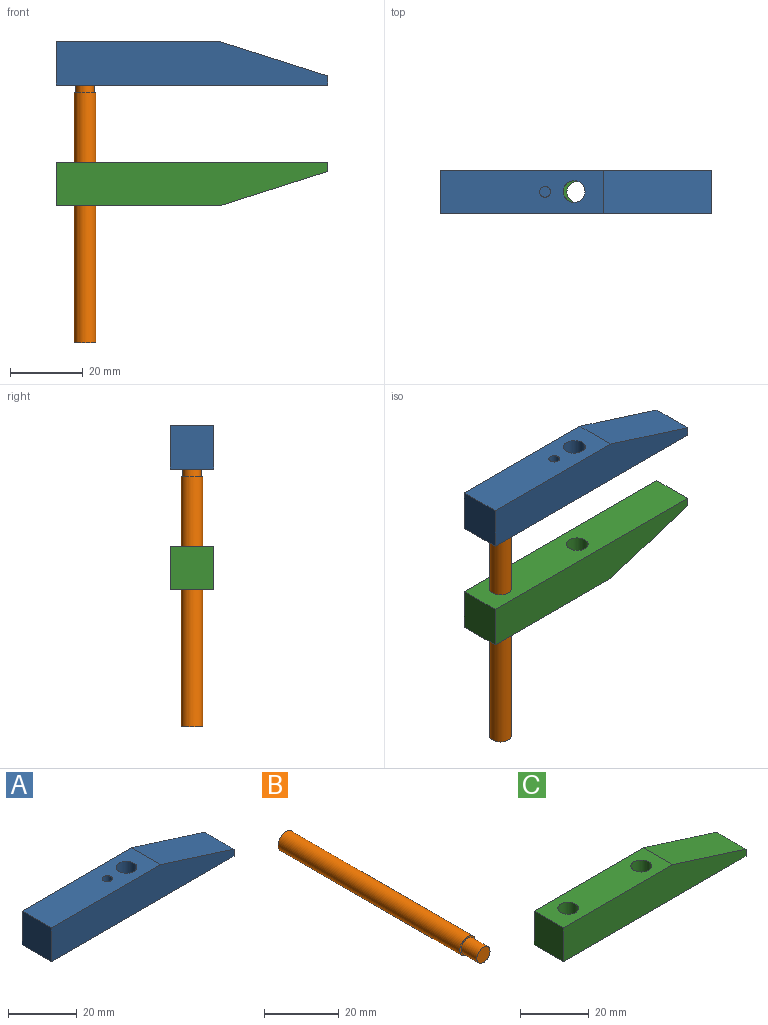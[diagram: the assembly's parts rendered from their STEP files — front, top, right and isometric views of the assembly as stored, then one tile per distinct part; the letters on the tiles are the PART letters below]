
ASSEMBLY  parts=3 mates=2
PART A: 12 faces, bbox 75x12x12 mm
  f0: plane 12x12mm, normal (-1,0,0), area 144mm2, adj f1,f4,f5,f6
  f1: plane 75x12mm, normal (0,0,-1), area 852.1mm2, adj f0,f2,f5,f6,f7,f11
  f2: plane 12x2.5mm, normal (1,0,0), area 30mm2, adj f1,f3,f5,f6
  f3: plane 30x12mm, normal (0.3,0,0.95), area 377.6mm2, adj f2,f4,f5,f6
  f4: plane 45x12mm, normal (0,0,1), area 504.7mm2, adj f0,f3,f5,f6,f9,f11
  f5: plane 75x12mm, normal (0,-1,0), area 757.5mm2, adj f0,f1,f2,f3,f4
  f6: plane 75x12mm, normal (0,1,0), area 757.5mm2, adj f0,f1,f2,f3,f4
  f7: cylinder r=2.5mm len=5mm, axis (0,0,-1), area 62.8mm2, adj f1,f8
  f8: plane 5x5mm, normal (0,0,-1), area 19.6mm2, adj f7
  f9: cylinder r=1.5mm len=5mm, axis (0,0,1), area 47.1mm2, adj f4,f10
  f10: plane 3x3mm, normal (0,0,1), area 7.1mm2, adj f9
  f11: cylinder r=3mm len=12mm, axis (0,0,1), area 226.2mm2, adj f1,f4
PART B: 5 faces, bbox 6x75x6 mm
  f0: cylinder r=3mm len=69mm, axis (0,1,0), area 1300.6mm2, adj f1,f2
  f1: plane 6x6mm, normal (0,-1,0), area 8.6mm2, adj f0,f3
  f2: plane 6x6mm, normal (0,1,0), area 28.3mm2, adj f0
  f3: cylinder r=2.5mm len=6mm, axis (0,1,0), area 94.2mm2, adj f1,f4
  f4: plane 5x5mm, normal (0,-1,0), area 19.6mm2, adj f3
PART C: 9 faces, bbox 75x12x12 mm
  f0: plane 30x12mm, normal (0.3,0,0.95), area 377.6mm2, adj f1,f4,f5,f6
  f1: plane 45x12mm, normal (0,0,1), area 483.5mm2, adj f0,f2,f5,f6,f7,f8
  f2: plane 12x12mm, normal (-1,0,0), area 144mm2, adj f1,f3,f5,f6
  f3: plane 75x12mm, normal (0,0,-1), area 843.5mm2, adj f2,f4,f5,f6,f7,f8
  f4: plane 12x2.5mm, normal (1,0,0), area 30mm2, adj f0,f3,f5,f6
  f5: plane 75x12mm, normal (0,-1,0), area 757.5mm2, adj f0,f1,f2,f3,f4
  f6: plane 75x12mm, normal (0,1,0), area 757.5mm2, adj f0,f1,f2,f3,f4
  f7: cylinder r=3mm len=12mm, axis (0,0,1), area 226.2mm2, adj f1,f3
  f8: cylinder r=3mm len=12mm, axis (0,0,1), area 226.2mm2, adj f1,f3
PLACE A t=(-11.41,-18.46,3.18)mm
PLACE B rot(axis=(-1,0,0),90deg) t=(-34.62,-24.46,-70.32)mm
PLACE C rot(axis=(-1,0,0),180deg) t=(-11.92,-30.46,-32.66)mm
MATE fastened B.f0 <-> A.f7  axis (0,0,1) through (-34.62,-24.46,4.68)mm
MATE slider C.f8 <-> B.f0  axis (0,0,1) through (-34.62,-24.46,-20.66)mm
